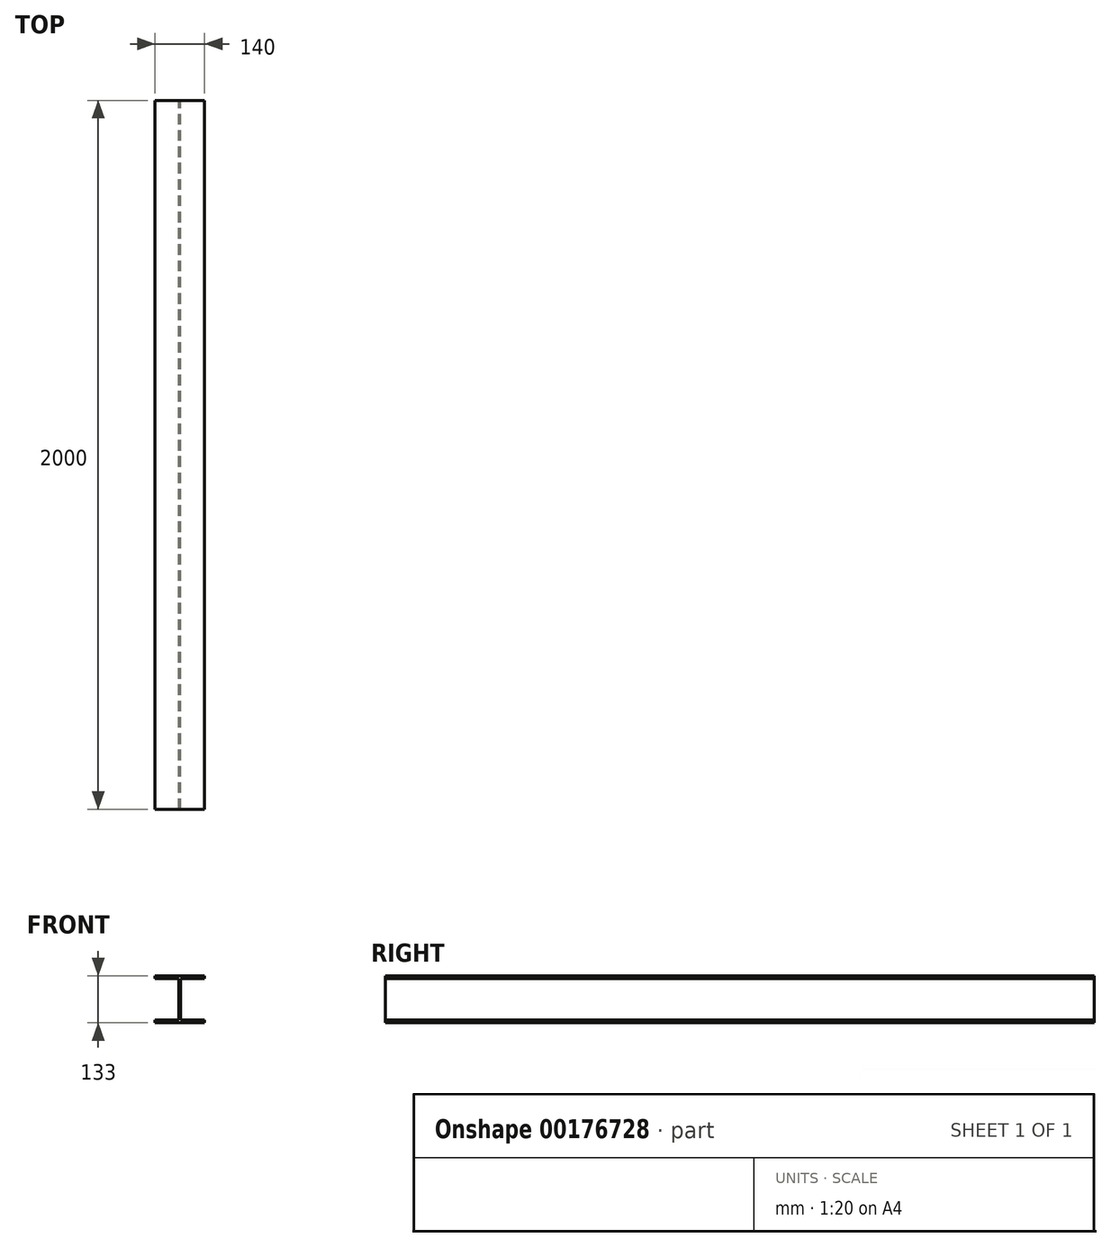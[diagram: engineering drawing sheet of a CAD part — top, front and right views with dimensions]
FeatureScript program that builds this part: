
annotation { "Feature Type Name" : "Feature", "Feature Type Description" : "" }
export const myFeature = defineFeature(function(context is Context, id is Id, definition is map)
    precondition{}
    {
        {
            var Q0;
            Q0=qCreatedBy(makeId("Front.planeOp"),FACE);
            var sketch = newSketch(context, id + "F0", { "sketchPlane" : qUnion([Q0])});
            skLineSegment(sketch, "E0", {"start": v(0, 0) * mm, "end": v(140, 0) * mm});
            skLineSegment(sketch, "E1", {"start": v(140, 0) * mm, "end": v(140, 8.5) * mm});
            skLineSegment(sketch, "E2", {"start": v(140, 8.5) * mm, "end": v(72.75, 8.5) * mm});
            skLineSegment(sketch, "E3", {"start": v(72.75, 8.5) * mm, "end": v(72.75, 124.5) * mm});
            skLineSegment(sketch, "E4", {"start": v(72.75, 124.5) * mm, "end": v(140, 124.5) * mm});
            skLineSegment(sketch, "E5", {"start": v(140, 124.5) * mm, "end": v(140, 133) * mm});
            skLineSegment(sketch, "E6", {"start": v(140, 133) * mm, "end": v(0, 133) * mm});
            skLineSegment(sketch, "E7", {"start": v(0, 133) * mm, "end": v(0, 124.5) * mm});
            skLineSegment(sketch, "E8", {"start": v(0, 124.5) * mm, "end": v(67.25, 124.5) * mm});
            skLineSegment(sketch, "E9", {"start": v(67.25, 124.5) * mm, "end": v(67.25, 8.5) * mm});
            skLineSegment(sketch, "E10", {"start": v(67.25, 8.5) * mm, "end": v(0, 8.5) * mm});
            skLineSegment(sketch, "E11", {"start": v(0, 8.5) * mm, "end": v(0, 0) * mm});
            skSolve(sketch);
        }
        {
            var Q0;
            Q0=makeQuery(id+"F0.imprint","IMPRINT",FACE,{"disambiguationData":[TD([[makeQuery(id+"F0.imprint","IMPRINT",EDGE,{"derivedFrom":sQuery(id+"F0.wireOp",EDGE,"E0")}),1.0]])]});
            extrude(context, id + "F1", {"entities" : qUnion([Q0]), "depth" : 2000 * mm});
        }
    });
